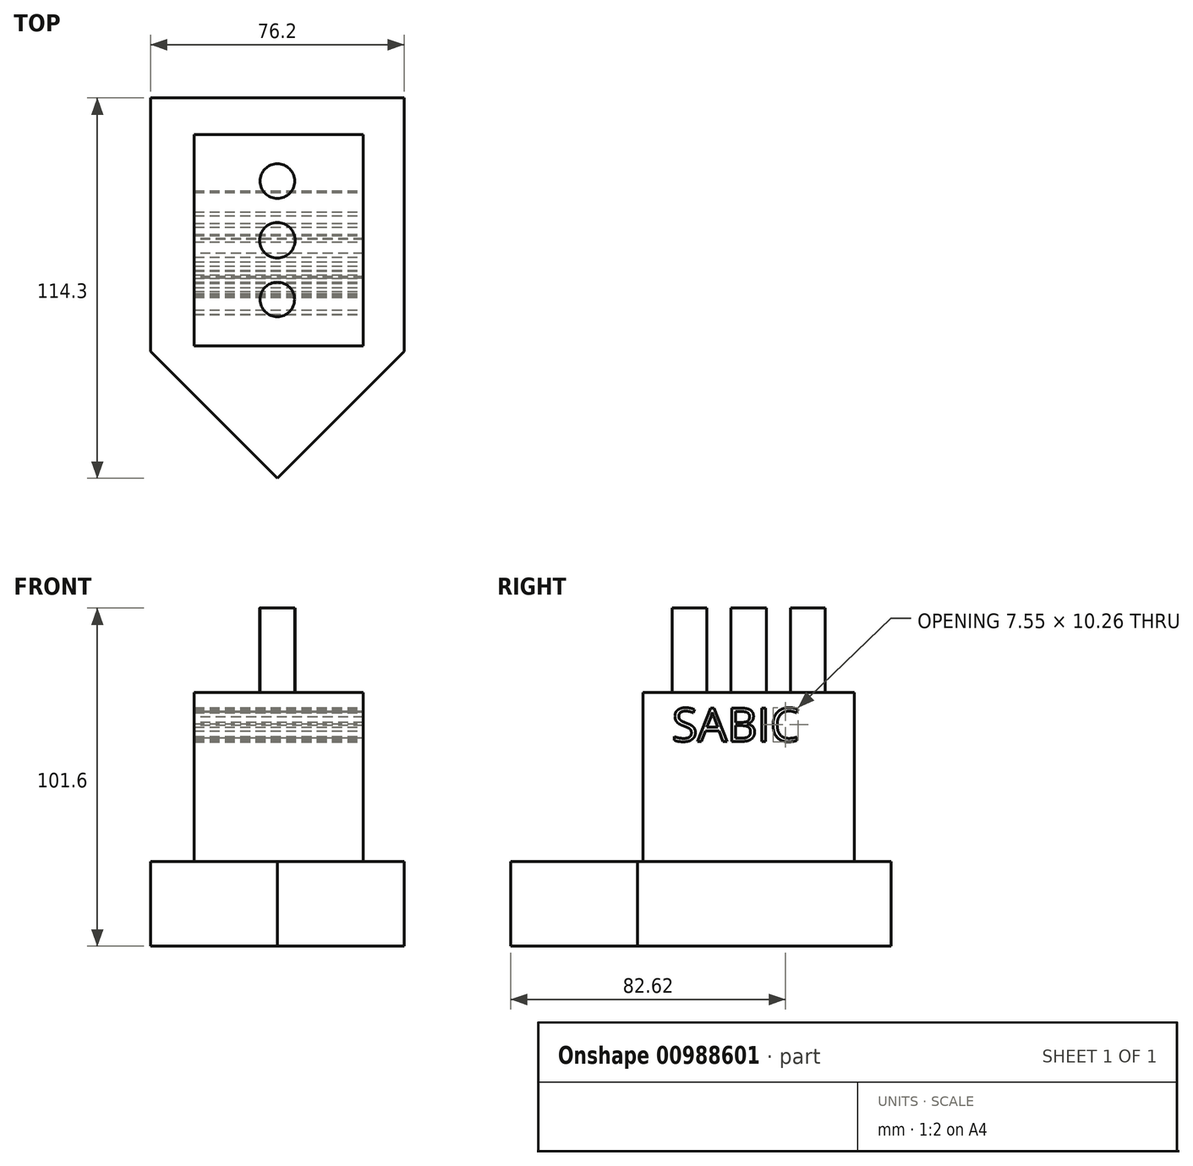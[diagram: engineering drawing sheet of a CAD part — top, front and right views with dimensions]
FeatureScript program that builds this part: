
annotation { "Feature Type Name" : "Feature", "Feature Type Description" : "" }
export const myFeature = defineFeature(function(context is Context, id is Id, definition is map)
    precondition{}
    {
        {
            var Q0;
            Q0=qCreatedBy(makeId("Top.planeOp"),FACE);
            var sketch = newSketch(context, id + "F0", { "sketchPlane" : qUnion([Q0])});
            skLineSegment(sketch, "E0", {"start": v(-38.1, 65.8) * mm, "end": v(-38.1, -10.4) * mm});
            skLineSegment(sketch, "E1", {"start": v(-38.1, -10.4) * mm, "end": v(0, -48.5) * mm});
            skLineSegment(sketch, "E2", {"start": v(0, -48.5) * mm, "end": v(38.1, -10.4) * mm});
            skLineSegment(sketch, "E3", {"start": v(38.1, -10.4) * mm, "end": v(38.1, 65.8) * mm});
            skLineSegment(sketch, "E4", {"start": v(38.1, 65.8) * mm, "end": v(-38.1, 65.8) * mm});
            skSolve(sketch);
        }
        {
            var Q0;
            Q0 = qSketchRegion(id + "F0", true);
            extrude(context, id + "F1", {"entities" : qUnion([Q0]), "depth" : 25.4 * mm, "offsetDistance" : 25.4 * mm});
        }
        {
            var Q0;
            Q0=makeQuery(id+"F1.opExtrude","CAP_FACE",FACE,{"disambiguationData":[OSD([sQuery(id+"F0.wireOp",EDGE,"E0"),sQuery(id+"F0.wireOp",EDGE,"E1"),sQuery(id+"F0.wireOp",EDGE,"E2"),sQuery(id+"F0.wireOp",EDGE,"E3"),sQuery(id+"F0.wireOp",EDGE,"E4")])],"isStart":false});
            var sketch = newSketch(context, id + "F2", { "sketchPlane" : qUnion([Q0])});
            skLineSegment(sketch, "E5.bottom", {"start": v(25.84, 54.77) * mm, "end": v(-24.96, 54.77) * mm});
            skLineSegment(sketch, "E5.top", {"start": v(25.84, -8.73) * mm, "end": v(-24.96, -8.73) * mm});
            skLineSegment(sketch, "E5.left", {"start": v(25.84, 54.77) * mm, "end": v(25.84, -8.73) * mm});
            skLineSegment(sketch, "E5.right", {"start": v(-24.96, 54.77) * mm, "end": v(-24.96, -8.73) * mm});
            skSolve(sketch);
        }
        {
            var Q0;
            Q0 = qSketchRegion(id + "F2", true);
            extrude(context, id + "F3", {"entities" : qUnion([Q0]), "operationType" : NewBodyOperationType.ADD, "depth" : 50.8 * mm, "offsetDistance" : 25.4 * mm});
        }
        {
            var Q0;
            Q0=makeQuery(id+"F3.opExtrude","CAP_FACE",FACE,{"disambiguationData":[OSD([sQuery(id+"F2.wireOp",EDGE,"E5.bottom"),sQuery(id+"F2.wireOp",EDGE,"E5.top"),sQuery(id+"F2.wireOp",EDGE,"E5.left"),sQuery(id+"F2.wireOp",EDGE,"E5.right")])],"isStart":false});
            var sketch = newSketch(context, id + "F4", { "sketchPlane" : qUnion([Q0])});
            skCircle(sketch, "E6", {"center": v(0, 40.8) * mm, "radius": 5.18 * mm});
            skCircle(sketch, "E7", {"center": v(0, 23.02) * mm, "radius": 5.32 * mm});
            skCircle(sketch, "E8", {"center": v(0, 5.24) * mm, "radius": 5.17 * mm});
            skSolve(sketch);
        }
        {
            var Q0;
            Q0 = qSketchRegion(id + "F4", true);
            extrude(context, id + "F5", {"entities" : qUnion([Q0]), "operationType" : NewBodyOperationType.ADD, "depth" : 25.4 * mm, "offsetDistance" : 25.4 * mm});
        }
        {
            var Q0;
            Q0=qCreatedBy(makeId("Right.planeOp"),FACE);
            var sketch = newSketch(context, id + "F6", { "sketchPlane" : qUnion([Q0])});
            skText(sketch, "E9", { "text": "SABIC", "fontName": "OpenSans-Regular.ttf"});
            const initialGuessF6  = {"E9": [0, 0.06156, 1, 0, 0.01007]};
            skSetInitialGuess(sketch, initialGuessF6);
            skSolve(sketch);
        }
        {
            var Q0;
            Q0 = qSketchRegion(id + "F6", true);
            extrude(context, id + "F7", {"entities" : qUnion([Q0]), "operationType" : NewBodyOperationType.REMOVE, "oppositeDirection" : true, "depth" : 50.8 * mm, "offsetDistance" : 25.4 * mm});
        }
        {
            var Q0;
            Q0 = qSketchRegion(id + "F6", true);
            extrude(context, id + "F8", {"entities" : qUnion([Q0]), "operationType" : NewBodyOperationType.REMOVE, "depth" : 90.42 * mm, "offsetDistance" : 25.4 * mm});
        }
    });
